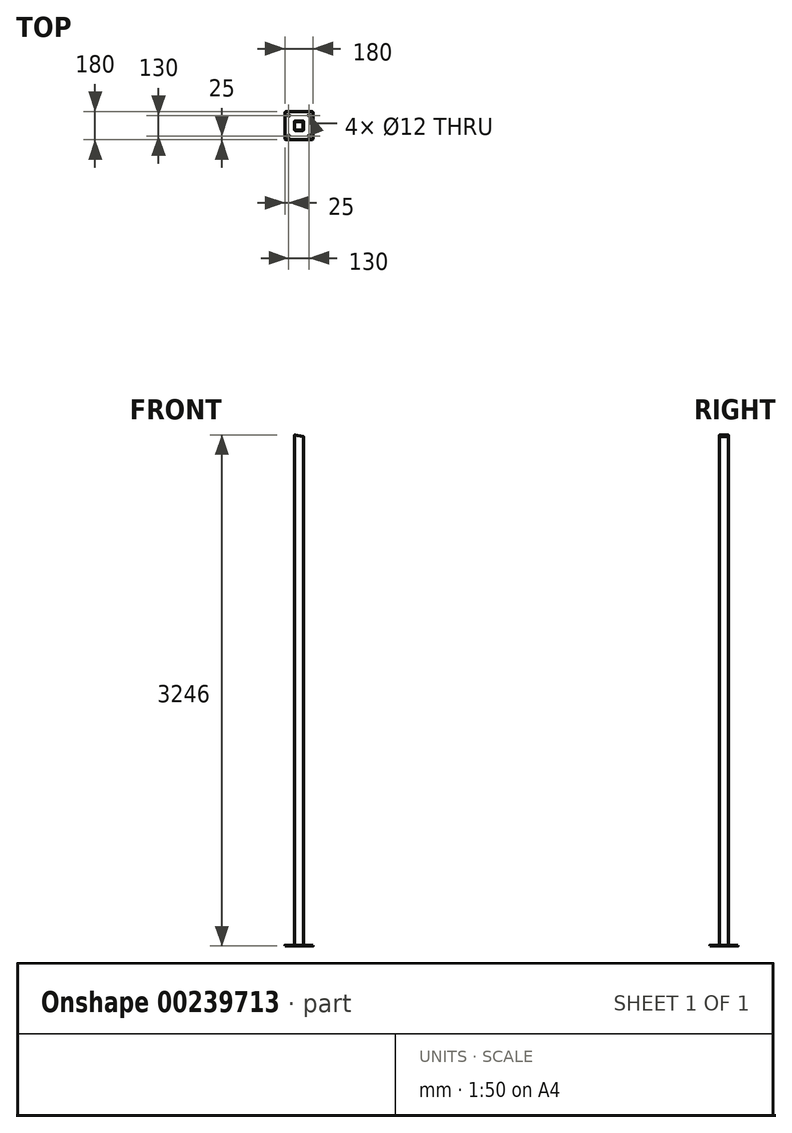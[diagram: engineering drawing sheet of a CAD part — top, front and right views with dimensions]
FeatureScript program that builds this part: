
annotation { "Feature Type Name" : "Feature", "Feature Type Description" : "" }
export const myFeature = defineFeature(function(context is Context, id is Id, definition is map)
    precondition{}
    {
        {
            var Q0;
            Q0=qCreatedBy(makeId("Top.planeOp"),FACE);
            var sketch = newSketch(context, id + "F0", { "sketchPlane" : qUnion([Q0])});
            skLineSegment(sketch, "E0.bottom", {"start": v(80, 90) * mm, "end": v(-80, 90) * mm});
            skLineSegment(sketch, "E0.top", {"start": v(80, -90) * mm, "end": v(-80, -90) * mm});
            skLineSegment(sketch, "E0.left", {"start": v(90, 80) * mm, "end": v(90, -80) * mm});
            skLineSegment(sketch, "E0.right", {"start": v(-90, 80) * mm, "end": v(-90, -80) * mm});
            skPoint(sketch, "E0.middle", {"position": v(0, 0) * mm});
            skPoint(sketch, "E1.visualSharp", {"position": v(-90, 90) * mm});
            skArc(sketch, "E1.filletArc", {"start": v(-80, 90) * mm, "mid": v(-87.07, 87.07) * mm, "end": v(-90, 80) * mm});
            skPoint(sketch, "E2.visualSharp", {"position": v(90, 90) * mm});
            skArc(sketch, "E2.filletArc", {"start": v(90, 80) * mm, "mid": v(87.07, 87.07) * mm, "end": v(80, 90) * mm});
            skPoint(sketch, "E3.visualSharp", {"position": v(90, -90) * mm});
            skArc(sketch, "E3.filletArc", {"start": v(80, -90) * mm, "mid": v(87.07, -87.07) * mm, "end": v(90, -80) * mm});
            skPoint(sketch, "E4.visualSharp", {"position": v(-90, -90) * mm});
            skArc(sketch, "E4.filletArc", {"start": v(-90, -80) * mm, "mid": v(-87.07, -87.07) * mm, "end": v(-80, -90) * mm});
            skCircle(sketch, "E5", {"center": v(-65, 65) * mm, "radius": 6 * mm});
            skCircle(sketch, "E6.0.1.0", {"center": v(-65, -65) * mm, "radius": 6 * mm});
            skCircle(sketch, "E6.1.0.0", {"center": v(65, 65) * mm, "radius": 6 * mm});
            skCircle(sketch, "E6.1.1.0", {"center": v(65, -65) * mm, "radius": 6 * mm});
            skLineSegment(sketch, "E6.direction1", {"start": v(-65, 65) * mm, "end": v(65, 65) * mm, "construction": true});
            skLineSegment(sketch, "E6.direction2", {"start": v(-65, 65) * mm, "end": v(-65, -65) * mm, "construction": true});
            skSolve(sketch);
        }
        {
            var Q0;
            Q0=makeQuery(id+"F0.imprint","IMPRINT",FACE,{"disambiguationData":[TD([[makeQuery(id+"F0.imprint","IMPRINT",EDGE,{"derivedFrom":sQuery(id+"F0.wireOp",EDGE,"E0.bottom")}),1.0]])]});
            extrude(context, id + "F1", {"entities" : qUnion([Q0]), "depth" : 6 * mm});
        }
        {
            var Q0;
            Q0=makeQuery(id+"F1.opExtrude","CAP_FACE",FACE,{"disambiguationData":[OSD([sQuery(id+"F0.wireOp",EDGE,"E0.bottom"),sQuery(id+"F0.wireOp",EDGE,"E0.top"),sQuery(id+"F0.wireOp",EDGE,"E0.left"),sQuery(id+"F0.wireOp",EDGE,"E0.right"),sQuery(id+"F0.wireOp",EDGE,"E1.filletArc"),sQuery(id+"F0.wireOp",EDGE,"E2.filletArc"),sQuery(id+"F0.wireOp",EDGE,"E3.filletArc"),sQuery(id+"F0.wireOp",EDGE,"E4.filletArc"),sQuery(id+"F0.wireOp",EDGE,"E5"),sQuery(id+"F0.wireOp",EDGE,"E6.0.1.0"),sQuery(id+"F0.wireOp",EDGE,"E6.1.0.0"),sQuery(id+"F0.wireOp",EDGE,"E6.1.1.0")])],"isStart":false});
            var sketch = newSketch(context, id + "F2", { "sketchPlane" : qUnion([Q0])});
            skLineSegment(sketch, "E7.bottom", {"start": v(25, -30) * mm, "end": v(-25, -30) * mm});
            skLineSegment(sketch, "E7.top", {"start": v(25, 30) * mm, "end": v(-25, 30) * mm});
            skLineSegment(sketch, "E7.left", {"start": v(30, -25) * mm, "end": v(30, 25) * mm});
            skLineSegment(sketch, "E7.right", {"start": v(-30, -25) * mm, "end": v(-30, 25) * mm});
            skPoint(sketch, "E7.middle", {"position": v(0, 0) * mm});
            skPoint(sketch, "E8.visualSharp", {"position": v(-30, 30) * mm});
            skArc(sketch, "E8.filletArc", {"start": v(-25, 30) * mm, "mid": v(-28.54, 28.54) * mm, "end": v(-30, 25) * mm});
            skPoint(sketch, "E9.visualSharp", {"position": v(30, 30) * mm});
            skArc(sketch, "E9.filletArc", {"start": v(30, 25) * mm, "mid": v(28.54, 28.54) * mm, "end": v(25, 30) * mm});
            skPoint(sketch, "E10.visualSharp", {"position": v(30, -30) * mm});
            skArc(sketch, "E10.filletArc", {"start": v(25, -30) * mm, "mid": v(28.54, -28.54) * mm, "end": v(30, -25) * mm});
            skPoint(sketch, "E11.visualSharp", {"position": v(-30, -30) * mm});
            skArc(sketch, "E11.filletArc", {"start": v(-30, -25) * mm, "mid": v(-28.54, -28.54) * mm, "end": v(-25, -30) * mm});
            skArc(sketch, "E12.0", {"start": v(27, 25) * mm, "mid": v(26.41, 26.41) * mm, "end": v(25, 27) * mm});
            skLineSegment(sketch, "E12.1", {"start": v(27, -25) * mm, "end": v(27, 25) * mm});
            skLineSegment(sketch, "E12.2", {"start": v(25, 27) * mm, "end": v(-25, 27) * mm});
            skArc(sketch, "E12.3", {"start": v(25, -27) * mm, "mid": v(26.41, -26.41) * mm, "end": v(27, -25) * mm});
            skArc(sketch, "E12.4", {"start": v(-25, 27) * mm, "mid": v(-26.41, 26.41) * mm, "end": v(-27, 25) * mm});
            skLineSegment(sketch, "E12.5", {"start": v(-27, -25) * mm, "end": v(-27, 25) * mm});
            skArc(sketch, "E12.6", {"start": v(-27, -25) * mm, "mid": v(-26.41, -26.41) * mm, "end": v(-25, -27) * mm});
            skLineSegment(sketch, "E12.7", {"start": v(25, -27) * mm, "end": v(-25, -27) * mm});
            skSolve(sketch);
        }
        {
            var Q0;
            Q0=makeQuery(id+"F2.imprint","IMPRINT",FACE,{"disambiguationData":[TD([[makeQuery(id+"F2.imprint","IMPRINT",EDGE,{"derivedFrom":sQuery(id+"F2.wireOp",EDGE,"E7.bottom")}),-1.0]])]});
            extrude(context, id + "F3", {"entities" : qUnion([Q0]), "operationType" : NewBodyOperationType.ADD, "depth" : 3240 * mm});
        }
        {
            var Q0;
            Q0=makeQuery(id+"F3.opExtrude","SWEPT_FACE",FACE,{"disambiguationData":[OSD([sQuery(id+"F2.wireOp",EDGE,"E7.bottom")])]});
            var sketch = newSketch(context, id + "F4", { "sketchPlane" : qUnion([Q0])});
            skLineSegment(sketch, "E13", {"start": v(-30.02, 3246) * mm, "end": v(31.37, 3246) * mm});
            skLineSegment(sketch, "E14", {"start": v(31.37, 3246) * mm, "end": v(31.37, 3235.17) * mm});
            skLineSegment(sketch, "E15", {"start": v(31.37, 3235.17) * mm, "end": v(-30.02, 3246) * mm});
            skSolve(sketch);
        }
        {
            var Q0;
            Q0 = qSketchRegion(id + "F4", true);
            extrude(context, id + "F5", {"entities" : qUnion([Q0]), "operationType" : NewBodyOperationType.REMOVE, "endBound" : BoundingType.THROUGH_ALL, "oppositeDirection" : true, "depth" : 25 * mm});
        }
        {
            var Q0;
            {var subQ0=sQuery(id+"F0.wireOp",EDGE,"E6.0.1.0");var subQ1=sQuery(id+"F0.wireOp",EDGE,"E4.filletArc");var subQ2=sQuery(id+"F0.wireOp",EDGE,"E3.filletArc");var subQ3=sQuery(id+"F0.wireOp",EDGE,"E2.filletArc");var subQ4=sQuery(id+"F0.wireOp",EDGE,"E1.filletArc");var subQ5=sQuery(id+"F0.wireOp",EDGE,"E0.bottom");var subQ6=sQuery(id+"F0.wireOp",EDGE,"E5");var subQ7=sQuery(id+"F0.wireOp",EDGE,"E0.top");var subQ8=sQuery(id+"F0.wireOp",EDGE,"E0.left");var subQ9=sQuery(id+"F0.wireOp",EDGE,"E0.right");var subQ10=sQuery(id+"F0.wireOp",EDGE,"E6.1.0.0");var subQ11=sQuery(id+"F0.wireOp",EDGE,"E6.1.1.0");Q0=makeQuery(id+"F3.boolean.opBoolean","SPLIT",FACE,{"disambiguationData":[TD([makeQuery(id+"F1.opExtrude","SWEPT_FACE",FACE,{"disambiguationData":[OSD([subQ5])]})])],"derivedFrom":makeQuery(id+"F1.opExtrude","CAP_FACE",FACE,{"disambiguationData":[OSD([subQ5,subQ7,subQ8,subQ9,subQ4,subQ3,subQ2,subQ1,subQ6,subQ0,subQ10,subQ11])],"isStart":false})});}
            cPlane(context, id + "F6", {"entities" : qUnion([Q0]), "cplaneType" : CPlaneType.OFFSET, "offset" : 0 * mm, "width" : 150 * mm, "height" : 150 * mm});
        }
    });
